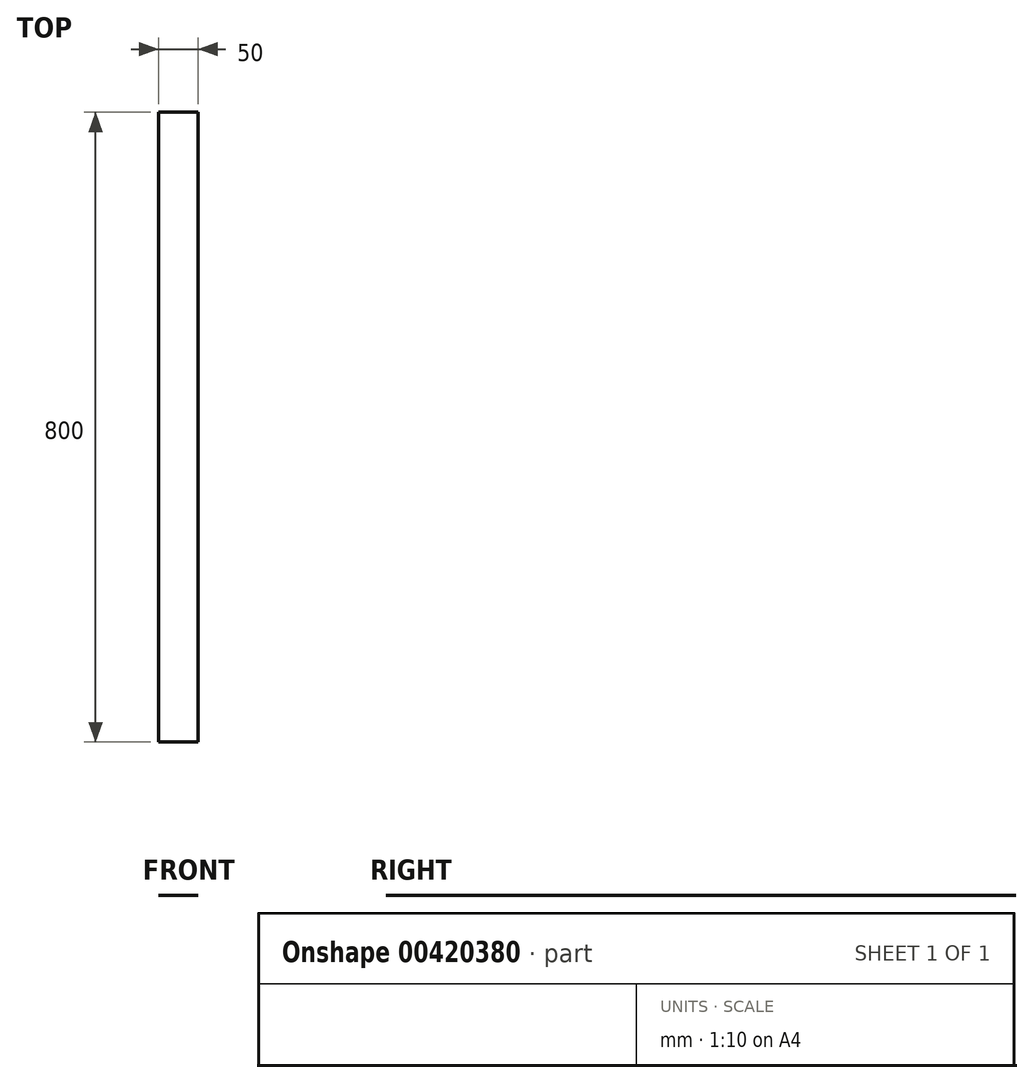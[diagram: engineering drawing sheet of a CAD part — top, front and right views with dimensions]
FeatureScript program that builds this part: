
annotation { "Feature Type Name" : "Feature", "Feature Type Description" : "" }
export const myFeature = defineFeature(function(context is Context, id is Id, definition is map)
    precondition{}
    {
        {
            var Q0;
            Q0=qCreatedBy(makeId("Front.planeOp"),FACE);
            var sketch = newSketch(context, id + "F0", { "sketchPlane" : qUnion([Q0])});
            skLineSegment(sketch, "E0.top", {"start": v(25, -6.14) * mm, "end": v(-25, -6.14) * mm});
            skPoint(sketch, "E0.middle", {"position": v(0, 0) * mm});
            skSolve(sketch);
        }
        {
            var Q0;
            Q0=qSketchRegion(id+"F0",true);
            var Q1;
            Q1=sQuery(id+"F0.wireOp",EDGE,"E0.right");
            var Q2;
            Q2=sQuery(id+"F0.wireOp",EDGE,"E0.top");
            var Q3;
            Q3=sQuery(id+"F0.wireOp",EDGE,"E0.left");
            extrude(context, id + "F1", {"entities" : qUnion([Q0]), "bodyType" : ToolBodyType.SURFACE, "operationType" : NewBodyOperationType.ADD, "surfaceEntities" : qUnion([Q1, Q2, Q3]), "endBound" : BoundingType.SYMMETRIC, "depth" : 800 * mm});
        }
    });
